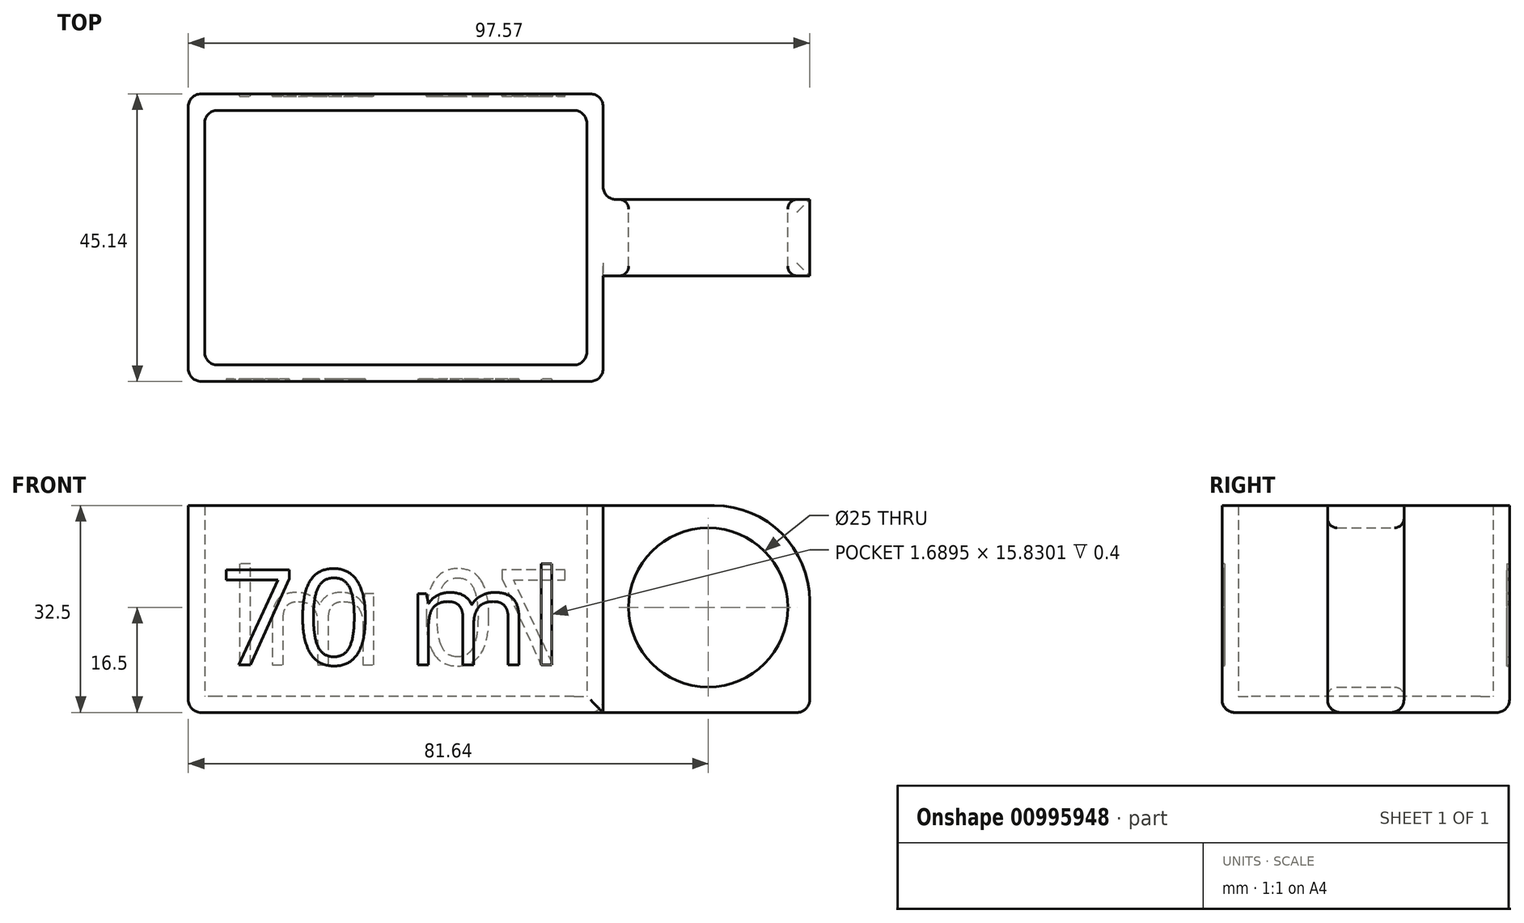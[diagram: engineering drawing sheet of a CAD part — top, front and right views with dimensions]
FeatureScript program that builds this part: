
annotation { "Feature Type Name" : "Feature", "Feature Type Description" : "" }
export const myFeature = defineFeature(function(context is Context, id is Id, definition is map)
    precondition{}
    {
        {
            var Q0;
            Q0=qCreatedBy(makeId("Top.planeOp"),FACE);
            var sketch = newSketch(context, id + "F0", { "sketchPlane" : qUnion([Q0])});
            skLineSegment(sketch, "E0.bottom", {"start": v(30, 20) * mm, "end": v(-30, 20) * mm});
            skLineSegment(sketch, "E0.top", {"start": v(30, -20) * mm, "end": v(-30, -20) * mm});
            skLineSegment(sketch, "E0.left", {"start": v(30, 20) * mm, "end": v(30, -20) * mm});
            skLineSegment(sketch, "E0.right", {"start": v(-30, 20) * mm, "end": v(-30, -20) * mm});
            skPoint(sketch, "E0.middle", {"position": v(0, 0) * mm});
            skLineSegment(sketch, "E1.0", {"start": v(-32.57, 22.57) * mm, "end": v(-32.57, -22.57) * mm});
            skLineSegment(sketch, "E1.1", {"start": v(32.57, 22.57) * mm, "end": v(-32.57, 22.57) * mm});
            skLineSegment(sketch, "E1.2", {"start": v(32.57, 22.57) * mm, "end": v(32.57, -22.57) * mm});
            skLineSegment(sketch, "E1.3", {"start": v(32.57, -22.57) * mm, "end": v(-32.57, -22.57) * mm});
            skSolve(sketch);
        }
        {
            var Q0;
            Q0=qSketchRegion(id+"F0",true);
            extrude(context, id + "F1", {"entities" : qUnion([Q0]), "depth" : 30 * mm, "offsetDistance" : 25 * mm});
        }
        {
            var Q0;
            Q0=makeQuery(id+"F0.imprint","IMPRINT",FACE,{"disambiguationData":[TD([[makeQuery(id+"F0.imprint","IMPRINT",EDGE,{"derivedFrom":sQuery(id+"F0.wireOp",EDGE,"E0.bottom")}),1.0]])]});
            var Q1;
            Q1=makeQuery(id+"F0.imprint","IMPRINT",FACE,{"disambiguationData":[TD([[makeQuery(id+"F0.imprint","IMPRINT",EDGE,{"derivedFrom":sQuery(id+"F0.wireOp",EDGE,"E0.bottom")}),-1.0]])]});
            extrude(context, id + "F2", {"entities" : qUnion([Q0, Q1]), "operationType" : NewBodyOperationType.ADD, "oppositeDirection" : true, "depth" : 2.5 * mm, "offsetDistance" : 25 * mm});
        }
        {
            var Q0;
            Q0=makeQuery(id+"F1.opExtrude","SWEPT_EDGE",EDGE,{"disambiguationData":[OSD([sQuery(id+"F0.wireOp",EDGE,"E0.bottom"),sQuery(id+"F0.wireOp",EDGE,"E0.right")])]});
            var Q1;
            Q1=makeQuery(id+"F1.opExtrude","CAP_EDGE",EDGE,{"disambiguationData":[OSD([sQuery(id+"F0.wireOp",EDGE,"E0.right")])],"isStart":true});
            var Q2;
            Q2=makeQuery(id+"F1.opExtrude","CAP_EDGE",EDGE,{"disambiguationData":[OSD([sQuery(id+"F0.wireOp",EDGE,"E0.bottom")])],"isStart":true});
            var Q3;
            Q3=makeQuery(id+"F1.opExtrude","SWEPT_EDGE",EDGE,{"disambiguationData":[OSD([sQuery(id+"F0.wireOp",EDGE,"E0.top"),sQuery(id+"F0.wireOp",EDGE,"E0.right")])]});
            var Q4;
            Q4=makeQuery(id+"F1.opExtrude","SWEPT_EDGE",EDGE,{"disambiguationData":[OSD([sQuery(id+"F0.wireOp",EDGE,"E0.bottom"),sQuery(id+"F0.wireOp",EDGE,"E0.left")])]});
            var Q5;
            Q5=makeQuery(id+"F1.opExtrude","CAP_EDGE",EDGE,{"disambiguationData":[OSD([sQuery(id+"F0.wireOp",EDGE,"E0.left")])],"isStart":true});
            var Q6;
            Q6=makeQuery(id+"F1.opExtrude","CAP_EDGE",EDGE,{"disambiguationData":[OSD([sQuery(id+"F0.wireOp",EDGE,"E0.top")])],"isStart":true});
            var Q7;
            Q7=makeQuery(id+"F1.opExtrude","SWEPT_EDGE",EDGE,{"disambiguationData":[OSD([sQuery(id+"F0.wireOp",EDGE,"E0.top"),sQuery(id+"F0.wireOp",EDGE,"E0.left")])]});
            var Q8;
            {var subQ0=sQuery(id+"F0.wireOp",EDGE,"E1.3");var subQ1=sQuery(id+"F0.wireOp",EDGE,"E1.2");Q8=makeQuery(id+"F2.boolean.opBoolean","MERGE",EDGE,{"derivedFrom":[makeQuery(id+"F1.opExtrude","SWEPT_EDGE",EDGE,{"disambiguationData":[OSD([subQ1,subQ0])]}),makeQuery(id+"F2.opExtrude","SWEPT_EDGE",EDGE,{"disambiguationData":[OSD([subQ1,subQ0])]})]});}
            var Q9;
            {var subQ0=sQuery(id+"F0.wireOp",EDGE,"E1.2");var subQ1=sQuery(id+"F0.wireOp",EDGE,"E1.1");Q9=makeQuery(id+"F2.boolean.opBoolean","MERGE",EDGE,{"derivedFrom":[makeQuery(id+"F1.opExtrude","SWEPT_EDGE",EDGE,{"disambiguationData":[OSD([subQ1,subQ0])]}),makeQuery(id+"F2.opExtrude","SWEPT_EDGE",EDGE,{"disambiguationData":[OSD([subQ1,subQ0])]})]});}
            var Q10;
            {var subQ0=sQuery(id+"F0.wireOp",EDGE,"E1.3");var subQ1=sQuery(id+"F0.wireOp",EDGE,"E1.0");Q10=makeQuery(id+"F2.boolean.opBoolean","MERGE",EDGE,{"derivedFrom":[makeQuery(id+"F1.opExtrude","SWEPT_EDGE",EDGE,{"disambiguationData":[OSD([subQ1,subQ0])]}),makeQuery(id+"F2.opExtrude","SWEPT_EDGE",EDGE,{"disambiguationData":[OSD([subQ1,subQ0])]})]});}
            var Q11;
            {var subQ0=sQuery(id+"F0.wireOp",EDGE,"E1.1");var subQ1=sQuery(id+"F0.wireOp",EDGE,"E1.0");Q11=makeQuery(id+"F2.boolean.opBoolean","MERGE",EDGE,{"derivedFrom":[makeQuery(id+"F1.opExtrude","SWEPT_EDGE",EDGE,{"disambiguationData":[OSD([subQ1,subQ0])]}),makeQuery(id+"F2.opExtrude","SWEPT_EDGE",EDGE,{"disambiguationData":[OSD([subQ1,subQ0])]})]});}
            var Q12;
            Q12=makeQuery(id+"F2.opExtrude","CAP_EDGE",EDGE,{"disambiguationData":[OSD([sQuery(id+"F0.wireOp",EDGE,"E1.3")])],"isStart":false});
            var Q13;
            Q13=makeQuery(id+"F2.opExtrude","CAP_EDGE",EDGE,{"disambiguationData":[OSD([sQuery(id+"F0.wireOp",EDGE,"E1.0")])],"isStart":false});
            var Q14;
            Q14=makeQuery(id+"F2.opExtrude","CAP_EDGE",EDGE,{"disambiguationData":[OSD([sQuery(id+"F0.wireOp",EDGE,"E1.1")])],"isStart":false});
            fillet(context, id + "F3", {"entities" : qUnion([Q0, Q1, Q2, Q3, Q4, Q5, Q6, Q7, Q8, Q9, Q10, Q11, Q12, Q13, Q14]), "radius" : 2 * mm, "tangentPropagation" : true, "allowEdgeOverflow" : false});
        }
        {
            var Q0;
            Q0=qCreatedBy(makeId("Front.planeOp"),FACE);
            var sketch = newSketch(context, id + "F4", { "sketchPlane" : qUnion([Q0])});
            skLineSegment(sketch, "E2.bottom", {"start": v(32.57, 30) * mm, "end": v(50, 30) * mm});
            skLineSegment(sketch, "E2.top", {"start": v(32.57, -2.5) * mm, "end": v(65, -2.5) * mm});
            skLineSegment(sketch, "E2.left", {"start": v(32.57, 30) * mm, "end": v(32.57, -2.5) * mm});
            skLineSegment(sketch, "E2.right", {"start": v(65, 15) * mm, "end": v(65, -2.5) * mm});
            skCircle(sketch, "E3", {"center": v(49.07, 14) * mm, "radius": 12.5 * mm});
            skPoint(sketch, "E4.visualSharp", {"position": v(65, 30) * mm});
            skArc(sketch, "E4.filletArc", {"start": v(65, 15) * mm, "mid": v(60.6, 25.6) * mm, "end": v(50, 30) * mm});
            skSolve(sketch);
        }
        {
            var Q0;
            Q0=makeQuery(id+"F4.imprint","IMPRINT",FACE,{"disambiguationData":[TD([[makeQuery(id+"F4.imprint","IMPRINT",EDGE,{"derivedFrom":sQuery(id+"F4.wireOp",EDGE,"E2.bottom")}),-1.0]])]});
            extrude(context, id + "F5", {"entities" : qUnion([Q0]), "operationType" : NewBodyOperationType.ADD, "endBound" : BoundingType.SYMMETRIC, "depth" : 12 * mm, "offsetDistance" : 25 * mm});
        }
        {
            var Q0;
            Q0=makeQuery(id+"F5.opExtrude","CAP_EDGE",EDGE,{"disambiguationData":[OSD([sQuery(id+"F4.wireOp",EDGE,"E2.left")])],"isStart":false});
            var Q1;
            Q1=makeQuery(id+"F5.opExtrude","CAP_EDGE",EDGE,{"disambiguationData":[OSD([sQuery(id+"F4.wireOp",EDGE,"E2.left")])],"isStart":true});
            var Q2;
            {var subQ0=sQuery(id+"F0.wireOp",EDGE,"E1.1");var subQ1=sQuery(id+"F0.wireOp",EDGE,"E1.2");Q2=makeQuery(id+"F5.boolean.opBoolean","SPLIT",EDGE,{"disambiguationData":[TD([makeQuery(id+"F3.opFillet","BLEND_FACE",FACE,{"disambiguationData":[OSD([subQ0])]})])],"derivedFrom":makeQuery(id+"F2.opExtrude","CAP_EDGE",EDGE,{"disambiguationData":[OSD([subQ1])],"isStart":false})});}
            var Q3;
            Q3=makeQuery(id+"F5.opExtrude","CAP_EDGE",EDGE,{"disambiguationData":[OSD([sQuery(id+"F4.wireOp",EDGE,"E2.top")])],"isStart":true});
            var Q4;
            Q4=makeQuery(id+"F5.opExtrude","CAP_EDGE",EDGE,{"disambiguationData":[OSD([sQuery(id+"F4.wireOp",EDGE,"E2.top")])],"isStart":false});
            var Q5;
            Q5=makeQuery(id+"F5.opExtrude","SWEPT_EDGE",EDGE,{"disambiguationData":[OSD([sQuery(id+"F4.wireOp",EDGE,"E2.top"),sQuery(id+"F4.wireOp",EDGE,"E2.right")])]});
            fillet(context, id + "F6", {"entities" : qUnion([Q0, Q1, Q2, Q3, Q4, Q5]), "radius" : 2 * mm, "tangentPropagation" : true, "allowEdgeOverflow" : false});
        }
        {
            var Q0;
            {var subQ0=sQuery(id+"F0.wireOp",EDGE,"E1.3");Q0=makeQuery(id+"F2.boolean.opBoolean","MERGE",FACE,{"derivedFrom":[makeQuery(id+"F1.opExtrude","SWEPT_FACE",FACE,{"disambiguationData":[OSD([subQ0])]}),makeQuery(id+"F2.opExtrude","SWEPT_FACE",FACE,{"disambiguationData":[OSD([subQ0])]})]});}
            var sketch = newSketch(context, id + "F7", { "sketchPlane" : qUnion([Q0])});
            skText(sketch, "E5", { "text": "70 ml", "fontName": "OpenSans-Regular.ttf"});
            const initialGuessF7  = {"E5": [-0.02757, 0.005, 1, 0, 0.015]};
            skSetInitialGuess(sketch, initialGuessF7);
            skSolve(sketch);
        }
        {
            var Q0;
            Q0=qSketchRegion(id+"F7",true);
            extrude(context, id + "F8", {"entities" : qUnion([Q0]), "operationType" : NewBodyOperationType.REMOVE, "oppositeDirection" : true, "depth" : 0.4 * mm, "offsetDistance" : 25 * mm});
        }
        {
            var Q0;
            {var subQ0=sQuery(id+"F0.wireOp",EDGE,"E1.1");Q0=makeQuery(id+"F2.boolean.opBoolean","MERGE",FACE,{"derivedFrom":[makeQuery(id+"F1.opExtrude","SWEPT_FACE",FACE,{"disambiguationData":[OSD([subQ0])]}),makeQuery(id+"F2.opExtrude","SWEPT_FACE",FACE,{"disambiguationData":[OSD([subQ0])]})]});}
            var sketch = newSketch(context, id + "F9", { "sketchPlane" : qUnion([Q0])});
            skText(sketch, "E6", { "text": "70 ml", "fontName": "OpenSans-Regular.ttf"});
            const initialGuessF9  = {"E6": [-0.02757, 0.005, 1, 0, 0.015]};
            skSetInitialGuess(sketch, initialGuessF9);
            skSolve(sketch);
        }
        {
            var Q0;
            Q0=qSketchRegion(id+"F9",true);
            extrude(context, id + "F10", {"entities" : qUnion([Q0]), "operationType" : NewBodyOperationType.REMOVE, "oppositeDirection" : true, "depth" : 0.4 * mm, "offsetDistance" : 25 * mm});
        }
        {
            var Q0;
            Q0=makeQuery(id+"F5.opExtrude","CAP_EDGE",EDGE,{"disambiguationData":[OSD([sQuery(id+"F4.wireOp",EDGE,"E3")])],"isStart":false});
            var Q1;
            Q1=makeQuery(id+"F5.opExtrude","SWEPT_FACE",FACE,{"disambiguationData":[OSD([sQuery(id+"F4.wireOp",EDGE,"E3")])]});
            fillet(context, id + "F11", {"entities" : qUnion([Q0, Q1]), "radius" : 1.5 * mm, "tangentPropagation" : true, "allowEdgeOverflow" : false});
        }
    });
